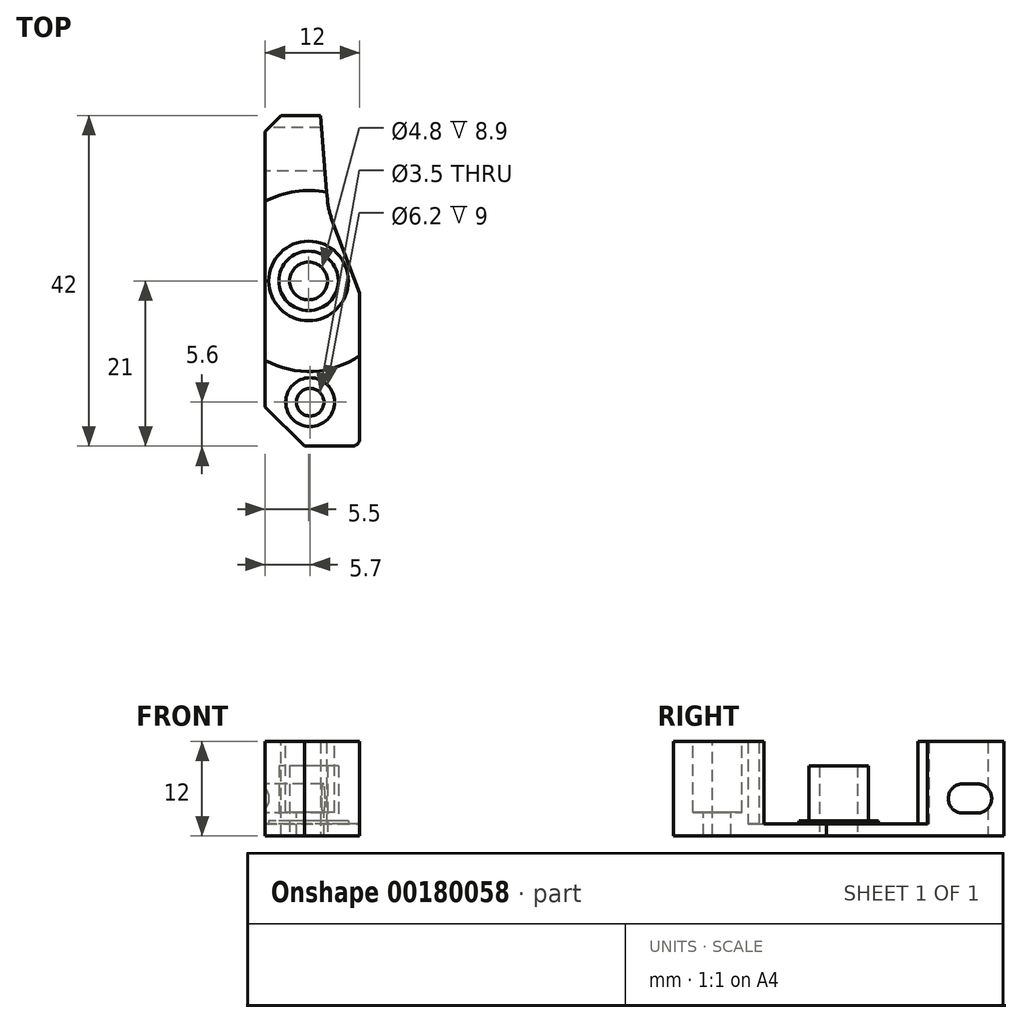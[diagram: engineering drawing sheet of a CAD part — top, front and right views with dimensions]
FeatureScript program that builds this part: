
annotation { "Feature Type Name" : "Feature", "Feature Type Description" : "" }
export const myFeature = defineFeature(function(context is Context, id is Id, definition is map)
    precondition{}
    {
        {
            var Q0;
            Q0=qCreatedBy(makeId("Top.planeOp"),FACE);
            cPlane(context, id + "F0", {"entities" : qUnion([Q0]), "cplaneType" : CPlaneType.OFFSET, "offset" : 1.5 * mm, "width" : 150 * mm, "height" : 150 * mm});
        }
        {
            var Q0;
            Q0=qCreatedBy(makeId("Top.planeOp"),FACE);
            var sketch = newSketch(context, id + "F1", { "sketchPlane" : qUnion([Q0])});
            skLineSegment(sketch, "E0.bottom", {"start": v(0, 0) * mm, "end": v(-12, 0) * mm});
            skLineSegment(sketch, "E0.top", {"start": v(0, 42) * mm, "end": v(-12, 42) * mm});
            skLineSegment(sketch, "E0.left", {"start": v(0, 0) * mm, "end": v(0, 42) * mm});
            skLineSegment(sketch, "E0.right", {"start": v(-12, 0) * mm, "end": v(-12, 42) * mm});
            skSolve(sketch);
        }
        {
            var Q0;
            Q0 = qSketchRegion(id + "F1", true);
            extrude(context, id + "F2", {"entities" : qUnion([Q0]), "depth" : 12 * mm});
        }
        {
            var Q0;
            {var subQ0=sQuery(id+"F1.wireOp",EDGE,"E0.bottom");var subQ1=sQuery(id+"F1.wireOp",EDGE,"E0.left");var subQ2=sQuery(id+"F1.wireOp",EDGE,"E0.right");Q0=makeQuery(id+"F9.boolean.opBoolean","SPLIT",FACE,{"disambiguationData":[TD([makeQuery(id+"F2.opExtrude","SWEPT_FACE",FACE,{"disambiguationData":[OSD([subQ0])]})])],"derivedFrom":makeQuery(id+"F2.opExtrude","CAP_FACE",FACE,{"disambiguationData":[OSD([subQ0,sQuery(id+"F1.wireOp",EDGE,"E0.top"),subQ1,subQ2])],"isStart":false})});}
            cPlane(context, id + "F3", {"entities" : qUnion([Q0]), "cplaneType" : CPlaneType.OFFSET, "offset" : 0 * mm, "width" : 150 * mm, "height" : 150 * mm});
        }
        {
            var Q0;
            Q0=makeQuery(id+"F2.opExtrude","SWEPT_FACE",FACE,{"disambiguationData":[OSD([sQuery(id+"F1.wireOp",EDGE,"E0.right")])]});
            cPlane(context, id + "F4", {"entities" : qUnion([Q0]), "cplaneType" : CPlaneType.OFFSET, "offset" : 0 * mm, "width" : 150 * mm, "height" : 150 * mm});
        }
        {
            var Q0;
            Q0=qCreatedBy(makeId("Top.planeOp"),FACE);
            var sketch = newSketch(context, id + "F5", { "sketchPlane" : qUnion([Q0])});
            skPoint(sketch, "E1", {"position": v(-6.5, 21) * mm});
            skSolve(sketch);
        }
        {
            var Q0;
            Q0=qCreatedBy(id+"F3.planeOp",FACE);
            var sketch = newSketch(context, id + "F6", { "sketchPlane" : qUnion([Q0])});
            skPoint(sketch, "E2", {"position": v(-6.3, 5.6) * mm});
            skSolve(sketch);
        }
        {
            var Q0;
            Q0=qCreatedBy(id+"F0.planeOp",FACE);
            var sketch = newSketch(context, id + "F7", { "sketchPlane" : qUnion([Q0])});
            skCircle(sketch, "E3", {"center": v(-6.5, 21) * mm, "radius": 11.5 * mm});
            skCircle(sketch, "E4", {"center": v(-6.5, 21) * mm, "radius": 3.78 * mm});
            skSolve(sketch);
        }
        {
            var Q0;
            Q0=qCreatedBy(id+"F0.planeOp",FACE);
            var sketch = newSketch(context, id + "F8", { "sketchPlane" : qUnion([Q0])});
            skCircle(sketch, "E5", {"center": v(-6.5, 21) * mm, "radius": 5.05 * mm});
            skSolve(sketch);
        }
        {
            var Q0;
            Q0 = qSketchRegion(id + "F7", true);
            extrude(context, id + "F9", {"entities" : qUnion([Q0]), "operationType" : NewBodyOperationType.REMOVE, "depth" : 25 * mm});
        }
        {
            var Q0;
            Q0 = qSketchRegion(id + "F8", true);
            extrude(context, id + "F10", {"entities" : qUnion([Q0]), "operationType" : NewBodyOperationType.ADD, "depth" : 0.4 * mm});
        }
        {
            var Q0;
            Q0=sQuery(id+"F5.wireOp",VERTEX,"E1");
            var Q1;
            Q1=makeQuery(id+"F2.opExtrude","SWEPT_BODY",BODY,{"disambiguationData":[OSD([sQuery(id+"F1.wireOp",EDGE,"E0.bottom"),sQuery(id+"F1.wireOp",EDGE,"E0.top"),sQuery(id+"F1.wireOp",EDGE,"E0.left"),sQuery(id+"F1.wireOp",EDGE,"E0.right")])]});
            hole(context, id + "F11", {"style" : HoleStyle.SIMPLE, "endStyle" : HoleEndStyle.THROUGH, "oppositeDirection" : true, "holeDiameter" : 4.8 * mm, "locations" : qUnion([Q0]), "scope" : qUnion([Q1]), "isTappedThrough" : true});
        }
        {
            var Q0;
            Q0=sQuery(id+"F6.wireOp",VERTEX,"E2");
            var Q1;
            Q1=makeQuery(id+"F2.opExtrude","SWEPT_BODY",BODY,{"disambiguationData":[OSD([sQuery(id+"F1.wireOp",EDGE,"E0.bottom"),sQuery(id+"F1.wireOp",EDGE,"E0.top"),sQuery(id+"F1.wireOp",EDGE,"E0.left"),sQuery(id+"F1.wireOp",EDGE,"E0.right")])]});
            hole(context, id + "F12", {"style" : HoleStyle.C_BORE, "endStyle" : HoleEndStyle.THROUGH, "holeDiameter" : 3.5 * mm, "cBoreDiameter" : 6.2 * mm, "cBoreDepth" : 9 * mm, "locations" : qUnion([Q0]), "scope" : qUnion([Q1]), "isTappedThrough" : true});
        }
        {
            var Q0;
            Q0=qCreatedBy(makeId("Top.planeOp"),FACE);
            var sketch = newSketch(context, id + "F13", { "sketchPlane" : qUnion([Q0])});
            skLineSegment(sketch, "E6", {"start": v(-4, 30) * mm, "end": v(-5, 42) * mm});
            skLineSegment(sketch, "E7", {"start": v(0, 42) * mm, "end": v(-5, 42) * mm});
            skLineSegment(sketch, "E8", {"start": v(-4, 30) * mm, "end": v(0, 19.47) * mm});
            skLineSegment(sketch, "E9", {"start": v(0, 42) * mm, "end": v(0, 19.47) * mm});
            skSolve(sketch);
        }
        {
            var Q0;
            Q0 = qSketchRegion(id + "F13", true);
            extrude(context, id + "F14", {"entities" : qUnion([Q0]), "operationType" : NewBodyOperationType.REMOVE, "depth" : 25 * mm});
        }
        {
            var Q0;
            Q0=qCreatedBy(id+"F4.planeOp",FACE);
            var sketch = newSketch(context, id + "F15", { "sketchPlane" : qUnion([Q0])});
            skLineSegment(sketch, "E10.bottom", {"start": v(-38.65, 6.6) * mm, "end": v(-36.75, 6.6) * mm});
            skLineSegment(sketch, "E10.top", {"start": v(-38.65, 2.9) * mm, "end": v(-36.75, 2.9) * mm});
            skLineSegment(sketch, "E10.left", {"start": v(-40.45, 4.8) * mm, "end": v(-40.45, 4.7) * mm});
            skLineSegment(sketch, "E10.right", {"start": v(-34.95, 4.8) * mm, "end": v(-34.95, 4.7) * mm});
            skPoint(sketch, "E11.visualSharp", {"position": v(-34.95, 6.6) * mm});
            skArc(sketch, "E11.filletArc", {"start": v(-34.95, 4.8) * mm, "mid": v(-35.48, 6.07) * mm, "end": v(-36.75, 6.6) * mm});
            skPoint(sketch, "E12.visualSharp", {"position": v(-34.95, 2.9) * mm});
            skArc(sketch, "E12.filletArc", {"start": v(-36.75, 2.9) * mm, "mid": v(-35.48, 3.43) * mm, "end": v(-34.95, 4.7) * mm});
            skPoint(sketch, "E13.visualSharp", {"position": v(-40.45, 2.9) * mm});
            skArc(sketch, "E13.filletArc", {"start": v(-40.45, 4.7) * mm, "mid": v(-39.92, 3.43) * mm, "end": v(-38.65, 2.9) * mm});
            skPoint(sketch, "E14.visualSharp", {"position": v(-40.45, 6.6) * mm});
            skArc(sketch, "E14.filletArc", {"start": v(-38.65, 6.6) * mm, "mid": v(-39.92, 6.07) * mm, "end": v(-40.45, 4.8) * mm});
            skSolve(sketch);
        }
        {
            var Q0;
            Q0 = qSketchRegion(id + "F15", true);
            extrude(context, id + "F16", {"entities" : qUnion([Q0]), "operationType" : NewBodyOperationType.REMOVE, "oppositeDirection" : true, "depth" : 25 * mm});
        }
        {
            var Q0;
            Q0=makeQuery(id+"F2.opExtrude","SWEPT_EDGE",EDGE,{"disambiguationData":[OSD([sQuery(id+"F1.wireOp",EDGE,"E0.bottom"),sQuery(id+"F1.wireOp",EDGE,"E0.right")])]});
            chamfer(context, id + "F17", {"entities" : qUnion([Q0]), "width" : 5 * mm, "tangentPropagation" : true});
        }
        {
            var Q0;
            Q0=makeQuery(id+"F2.opExtrude","SWEPT_EDGE",EDGE,{"disambiguationData":[OSD([sQuery(id+"F1.wireOp",EDGE,"E0.top"),sQuery(id+"F1.wireOp",EDGE,"E0.right")])]});
            chamfer(context, id + "F18", {"entities" : qUnion([Q0]), "width" : 2 * mm, "tangentPropagation" : true});
        }
        {
            var Q0;
            Q0=makeQuery(id+"F2.opExtrude","SWEPT_EDGE",EDGE,{"disambiguationData":[OSD([sQuery(id+"F1.wireOp",EDGE,"E0.bottom"),sQuery(id+"F1.wireOp",EDGE,"E0.left")])]});
            var Q1;
            Q1=makeQuery(id+"F14.boolean.opBoolean","COPY",EDGE,{"derivedFrom":makeQuery(id+"F14.opExtrude","SWEPT_EDGE",EDGE,{"disambiguationData":[OSD([sQuery(id+"F13.wireOp",EDGE,"E6"),sQuery(id+"F13.wireOp",EDGE,"E7")])]})});
            fillet(context, id + "F19", {"entities" : qUnion([Q0, Q1]), "radius" : 1 * mm, "tangentPropagation" : true, "allowEdgeOverflow" : false});
        }
        {
            var Q0;
            Q0=qCreatedBy(id+"F3.planeOp",FACE);
            var sketch = newSketch(context, id + "F20", { "sketchPlane" : qUnion([Q0])});
            skCircle(sketch, "E15", {"center": v(-6.5, 21) * mm, "radius": 4.5 * mm});
            skSolve(sketch);
        }
        {
            var Q0;
            Q0 = qSketchRegion(id + "F20", true);
            extrude(context, id + "F21", {"entities" : qUnion([Q0]), "operationType" : NewBodyOperationType.REMOVE, "oppositeDirection" : true, "depth" : 3.1 * mm});
        }
        {
            var Q0;
            Q0=makeQuery(id+"F14.boolean.opBoolean","COPY",EDGE,{"derivedFrom":makeQuery(id+"F14.opExtrude","SWEPT_EDGE",EDGE,{"disambiguationData":[OSD([sQuery(id+"F13.wireOp",EDGE,"E6"),sQuery(id+"F13.wireOp",EDGE,"E8")])]})});
            var Q1;
            Q1=makeQuery(id+"F14.boolean.opBoolean","COPY",EDGE,{"derivedFrom":makeQuery(id+"F14.opExtrude","SWEPT_EDGE",EDGE,{"disambiguationData":[OSD([sQuery(id+"F13.wireOp",EDGE,"E8"),sQuery(id+"F13.wireOp",EDGE,"E9")])]})});
            fillet(context, id + "F22", {"entities" : qUnion([Q0, Q1]), "radius" : 10 * mm, "tangentPropagation" : true, "allowEdgeOverflow" : false});
        }
    });
